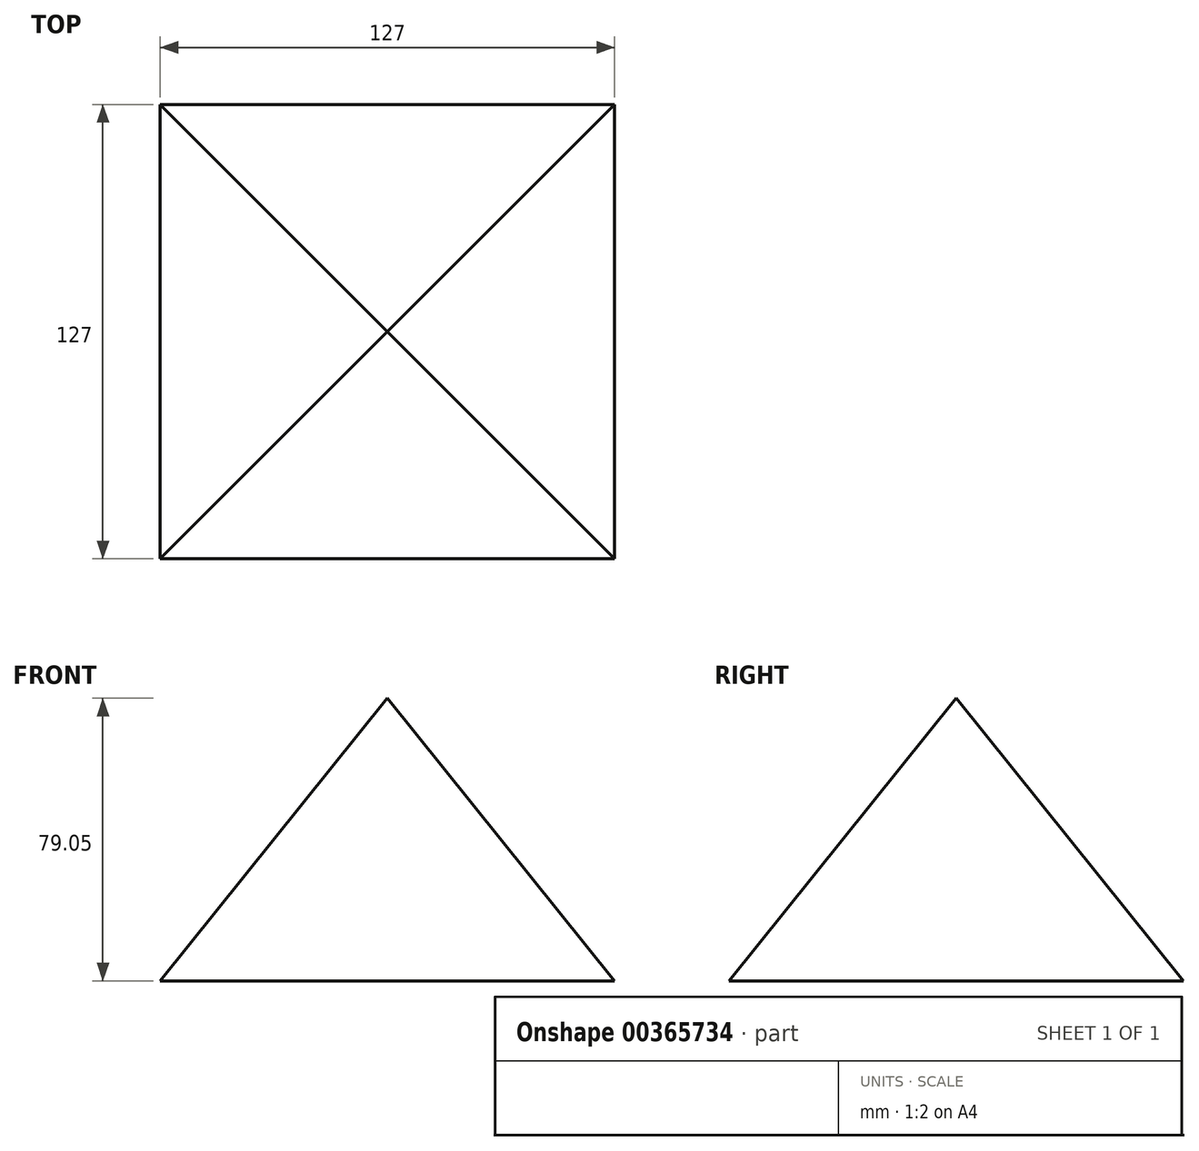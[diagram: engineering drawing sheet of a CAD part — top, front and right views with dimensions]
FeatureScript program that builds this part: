
annotation { "Feature Type Name" : "Feature", "Feature Type Description" : "" }
export const myFeature = defineFeature(function(context is Context, id is Id, definition is map)
    precondition{}
    {
        {
            var Q0;
            Q0=qCreatedBy(makeId("Top.planeOp"),FACE);
            var sketch = newSketch(context, id + "F0", { "sketchPlane" : qUnion([Q0])});
            skLineSegment(sketch, "E0.bottom", {"start": v(63.5, 63.5) * mm, "end": v(-63.5, 63.5) * mm});
            skLineSegment(sketch, "E0.top", {"start": v(63.5, -63.5) * mm, "end": v(-63.5, -63.5) * mm});
            skLineSegment(sketch, "E0.left", {"start": v(63.5, 63.5) * mm, "end": v(63.5, -63.5) * mm});
            skLineSegment(sketch, "E0.right", {"start": v(-63.5, 63.5) * mm, "end": v(-63.5, -63.5) * mm});
            skPoint(sketch, "E0.middle", {"position": v(0, 0) * mm});
            skSolve(sketch);
        }
        {
            var Q0;
            Q0=qCreatedBy(makeId("Right.planeOp"),FACE);
            var sketch = newSketch(context, id + "F1", { "sketchPlane" : qUnion([Q0])});
            skPoint(sketch, "E1", {"position": v(0, 79.05) * mm});
            skSolve(sketch);
        }
        {
            var Q0;
            Q0=sQuery(id+"F1.wireOp",VERTEX,"E1");
            var Q1;
            Q1=makeQuery(id+"F0.imprint","IMPRINT",FACE,{"disambiguationData":[TD([[makeQuery(id+"F0.imprint","IMPRINT",EDGE,{"derivedFrom":sQuery(id+"F0.wireOp",EDGE,"E0.bottom")}),1.0]])]});
            loft(context, id + "F2", {"sheetProfilesArray" : [{ "sheetProfileEntities" : qUnion([Q0]) }, { "sheetProfileEntities" : qUnion([Q1]) }]});
        }
    });
